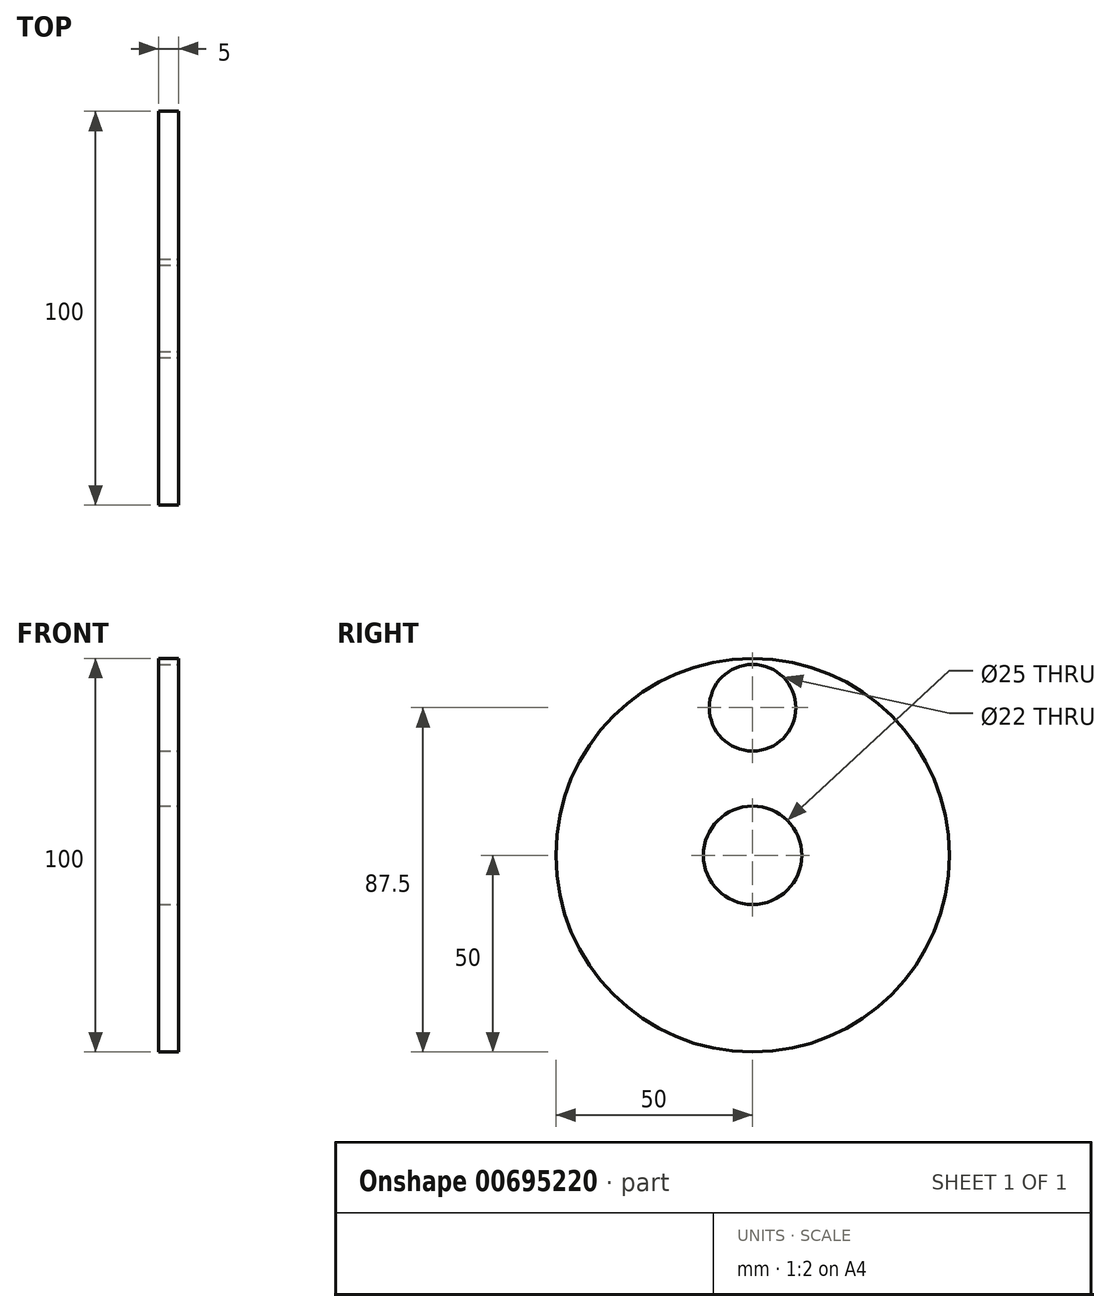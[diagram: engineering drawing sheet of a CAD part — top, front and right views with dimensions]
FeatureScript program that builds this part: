
annotation { "Feature Type Name" : "Feature", "Feature Type Description" : "" }
export const myFeature = defineFeature(function(context is Context, id is Id, definition is map)
    precondition{}
    {
        {
            var Q0;
            Q0=qCreatedBy(makeId("Right.planeOp"),FACE);
            var sketch = newSketch(context, id + "F0", { "sketchPlane" : qUnion([Q0])});
            skCircle(sketch, "E0", {"center": v(0, 0) * mm, "radius": 50 * mm});
            skSolve(sketch);
        }
        {
            var Q0;
            Q0=qSketchRegion(id+"F0",true);
            extrude(context, id + "F1", {"entities" : qUnion([Q0]), "endBound" : BoundingType.SYMMETRIC, "depth" : 5 * mm});
        }
        {
            var Q0;
            Q0=makeQuery(id+"F1.opExtrude","CAP_FACE",FACE,{"disambiguationData":[OSD([sQuery(id+"F0.wireOp",EDGE,"E0")])],"isStart":false});
            var sketch = newSketch(context, id + "F2", { "sketchPlane" : qUnion([Q0])});
            skPoint(sketch, "E1", {"position": v(0, 0) * mm});
            skSolve(sketch);
        }
        {
            var Q0;
            Q0=sQuery(id+"F2.wireOp",VERTEX,"E1");
            var Q1;
            Q1=makeQuery(id+"F1.opExtrude","SWEPT_BODY",BODY,{"disambiguationData":[OSD([sQuery(id+"F0.wireOp",EDGE,"E0")])]});
            hole(context, id + "F3", {"style" : HoleStyle.SIMPLE, "endStyle" : HoleEndStyle.THROUGH, "holeDiameter" : 25 * mm, "isTappedThrough" : true, "tappedDepth" : 12 * mm, "tapClearance" : 3, "locations" : qUnion([Q0]), "scope" : qUnion([Q1])});
        }
        {
            var Q0;
            Q0=makeQuery(id+"F1.opExtrude","CAP_FACE",FACE,{"disambiguationData":[OSD([sQuery(id+"F0.wireOp",EDGE,"E0")])],"isStart":false});
            var sketch = newSketch(context, id + "F4", { "sketchPlane" : qUnion([Q0])});
            skCircle(sketch, "E2", {"center": v(0, 0) * mm, "radius": 25 * mm, "construction": true});
            skCircle(sketch, "E3.0", {"center": v(0, 0) * mm, "radius": 50 * mm, "construction": true});
            skLineSegment(sketch, "E4", {"start": v(0, 50) * mm, "end": v(0, 25) * mm, "construction": true});
            skPoint(sketch, "E5", {"position": v(0, 37.5) * mm});
            skSolve(sketch);
        }
        {
            var Q0;
            Q0=sQuery(id+"F4.wireOp",VERTEX,"E5");
            var Q1;
            Q1=makeQuery(id+"F1.opExtrude","SWEPT_BODY",BODY,{"disambiguationData":[OSD([sQuery(id+"F0.wireOp",EDGE,"E0")])]});
            hole(context, id + "F5", {"style" : HoleStyle.SIMPLE, "endStyle" : HoleEndStyle.THROUGH, "holeDiameter" : 22 * mm, "isTappedThrough" : true, "tappedDepth" : 12 * mm, "tapClearance" : 3, "locations" : qUnion([Q0]), "scope" : qUnion([Q1])});
        }
    });
